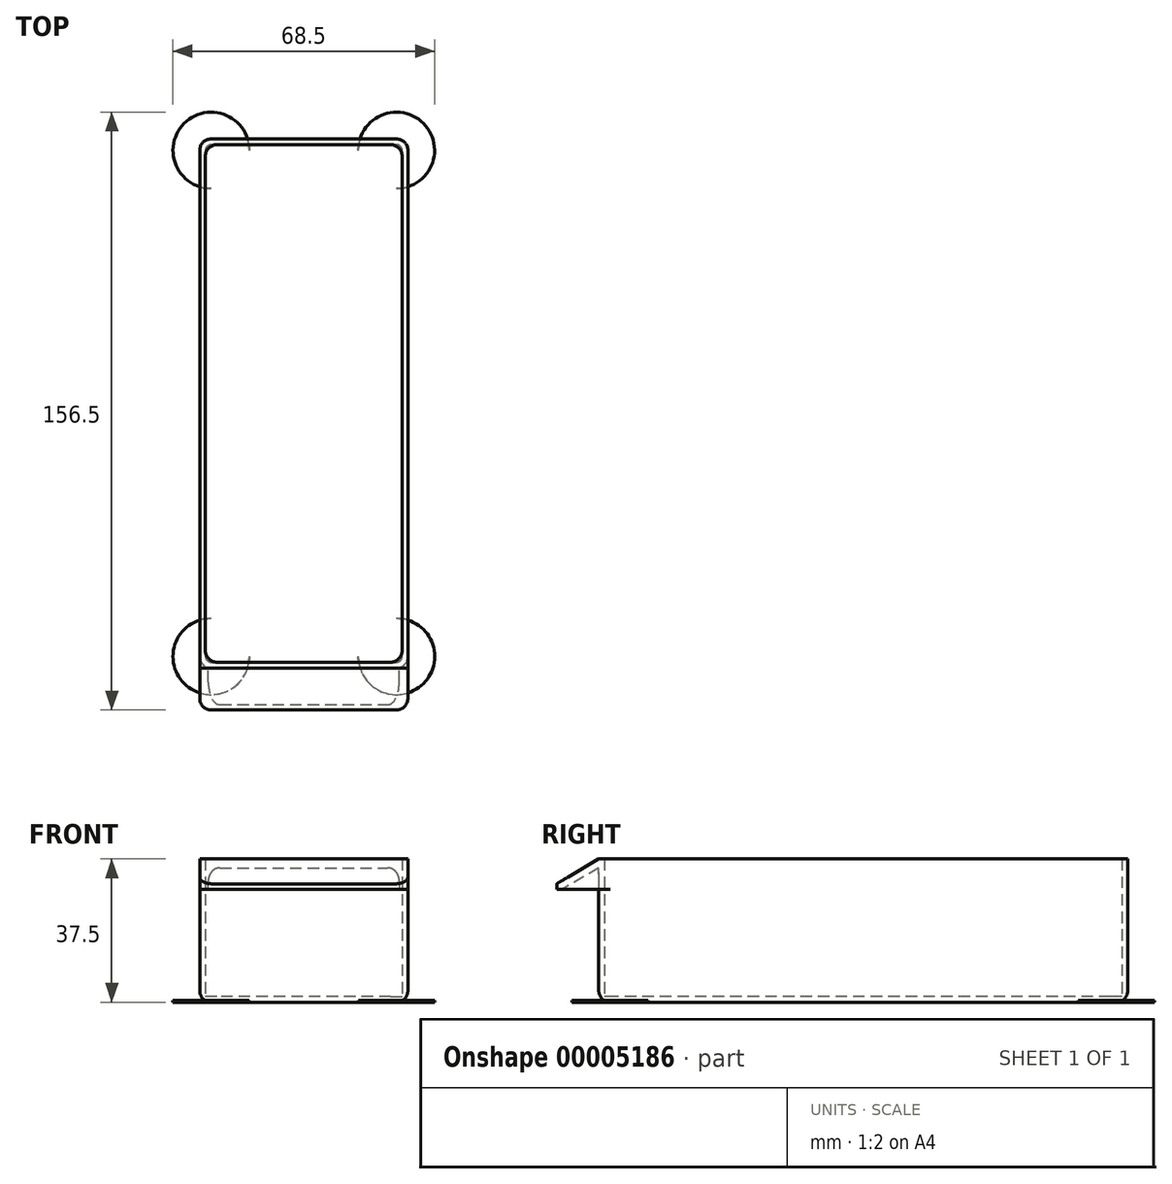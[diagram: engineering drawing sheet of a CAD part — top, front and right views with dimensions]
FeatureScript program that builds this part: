
annotation { "Feature Type Name" : "Feature", "Feature Type Description" : "" }
export const myFeature = defineFeature(function(context is Context, id is Id, definition is map)
    precondition{}
    {
        {
            var Q0;
            Q0=qCreatedBy(makeId("Top.planeOp"),FACE);
            var sketch = newSketch(context, id + "F0", { "sketchPlane" : qUnion([Q0])});
            skLineSegment(sketch, "E0.bottom", {"start": v(27.25, 69.25) * mm, "end": v(-27.25, 69.25) * mm});
            skLineSegment(sketch, "E0.top", {"start": v(27.25, -69.25) * mm, "end": v(-27.25, -69.25) * mm});
            skLineSegment(sketch, "E0.left", {"start": v(27.25, 69.25) * mm, "end": v(27.25, -69.25) * mm});
            skLineSegment(sketch, "E0.right", {"start": v(-27.25, 69.25) * mm, "end": v(-27.25, -69.25) * mm});
            skPoint(sketch, "E0.middle", {"position": v(0, 0) * mm});
            skSolve(sketch);
        }
        {
            var Q0;
            Q0 = qSketchRegion(id + "F0", true);
            extrude(context, id + "F1", {"entities" : qUnion([Q0]), "depth" : 1.5 * mm});
        }
        {
            var Q0;
            Q0=makeQuery(id+"F1.opExtrude","CAP_FACE",FACE,{"disambiguationData":[OSD([sQuery(id+"F0.wireOp",EDGE,"E0.bottom"),sQuery(id+"F0.wireOp",EDGE,"E0.top"),sQuery(id+"F0.wireOp",EDGE,"E0.left"),sQuery(id+"F0.wireOp",EDGE,"E0.right")])],"isStart":false});
            var sketch = newSketch(context, id + "F2", { "sketchPlane" : qUnion([Q0])});
            skLineSegment(sketch, "E1.0", {"start": v(27.25, 69.25) * mm, "end": v(-27.25, 69.25) * mm});
            skLineSegment(sketch, "E1.1", {"start": v(-27.25, 69.25) * mm, "end": v(-27.25, -69.25) * mm});
            skLineSegment(sketch, "E1.2", {"start": v(27.25, 69.25) * mm, "end": v(27.25, -69.25) * mm});
            skLineSegment(sketch, "E1.3", {"start": v(27.25, -69.25) * mm, "end": v(-27.25, -69.25) * mm});
            skLineSegment(sketch, "E2.bottom", {"start": v(25.75, 67.75) * mm, "end": v(-25.75, 67.75) * mm});
            skLineSegment(sketch, "E2.top", {"start": v(25.75, -67.75) * mm, "end": v(-25.75, -67.75) * mm});
            skLineSegment(sketch, "E2.left", {"start": v(25.75, 67.75) * mm, "end": v(25.75, -67.75) * mm});
            skLineSegment(sketch, "E2.right", {"start": v(-25.75, 67.75) * mm, "end": v(-25.75, -67.75) * mm});
            skPoint(sketch, "E2.middle", {"position": v(0, 0) * mm});
            skSolve(sketch);
        }
        {
            var Q0;
            Q0 = qSketchRegion(id + "F2", true);
            extrude(context, id + "F3", {"entities" : qUnion([Q0]), "operationType" : NewBodyOperationType.ADD, "depth" : 36 * mm});
        }
        {
            var Q0;
            Q0=makeQuery(id+"F3.boolean.opBoolean","MERGE",FACE,{"derivedFrom":[makeQuery(id+"F1.opExtrude","SWEPT_FACE",FACE,{"disambiguationData":[OSD([sQuery(id+"F0.wireOp",EDGE,"E0.right")])]}),makeQuery(id+"F3.opExtrude","SWEPT_FACE",FACE,{"disambiguationData":[OSD([sQuery(id+"F2.wireOp",EDGE,"E1.1")])]})]});
            var sketch = newSketch(context, id + "F4", { "sketchPlane" : qUnion([Q0])});
            skLineSegment(sketch, "E3", {"start": v(69.25, 37.5) * mm, "end": v(80.25, 31) * mm});
            skLineSegment(sketch, "E4", {"start": v(80.25, 31) * mm, "end": v(80.25, 29.5) * mm});
            skLineSegment(sketch, "E5", {"start": v(80.25, 29.5) * mm, "end": v(69.25, 29.5) * mm});
            skLineSegment(sketch, "E6", {"start": v(69.25, 29.5) * mm, "end": v(69.25, 37.5) * mm});
            skSolve(sketch);
        }
        {
            var Q0;
            Q0 = qSketchRegion(id + "F4", true);
            var Q1;
            Q1=makeQuery(id+"F3.boolean.opBoolean","MERGE",FACE,{"derivedFrom":[makeQuery(id+"F1.opExtrude","SWEPT_FACE",FACE,{"disambiguationData":[OSD([sQuery(id+"F0.wireOp",EDGE,"E0.left")])]}),makeQuery(id+"F3.opExtrude","SWEPT_FACE",FACE,{"disambiguationData":[OSD([sQuery(id+"F2.wireOp",EDGE,"E1.2")])]})]});
            extrude(context, id + "F5", {"entities" : qUnion([Q0]), "operationType" : NewBodyOperationType.ADD, "endBound" : BoundingType.UP_TO_SURFACE, "oppositeDirection" : true, "endBoundEntityFace" : qUnion([Q1]), "depth" : 25 * mm});
        }
        {
            var Q0;
            Q0=qCreatedBy(makeId("Right.planeOp"),FACE);
            var sketch = newSketch(context, id + "F6", { "sketchPlane" : qUnion([Q0])});
            skLineSegment(sketch, "E7.0", {"start": v(-69.25, 37.5) * mm, "end": v(-80.25, 31) * mm, "construction": true});
            skLineSegment(sketch, "E7.1", {"start": v(-80.25, 29.5) * mm, "end": v(-69.25, 29.5) * mm, "construction": true});
            skLineSegment(sketch, "E8", {"start": v(-69.25, 35.18) * mm, "end": v(-78.86, 29.5) * mm});
            skLineSegment(sketch, "E9", {"start": v(-78.86, 29.5) * mm, "end": v(-69.25, 29.5) * mm});
            skLineSegment(sketch, "E10", {"start": v(-69.25, 35.18) * mm, "end": v(-69.25, 29.5) * mm});
            skSolve(sketch);
        }
        {
            var Q0;
            Q0 = qSketchRegion(id + "F6", true);
            extrude(context, id + "F7", {"entities" : qUnion([Q0]), "operationType" : NewBodyOperationType.REMOVE, "oppositeDirection" : true, "depth" : 50 * mm, "symmetric" : true});
        }
        {
            var Q0;
            Q0=makeQuery(id+"F3.boolean.opBoolean","MERGE",EDGE,{"derivedFrom":[makeQuery(id+"F1.opExtrude","SWEPT_EDGE",EDGE,{"disambiguationData":[OSD([sQuery(id+"F0.wireOp",EDGE,"E0.top"),sQuery(id+"F0.wireOp",EDGE,"E0.right")])]}),makeQuery(id+"F3.opExtrude","SWEPT_EDGE",EDGE,{"disambiguationData":[OSD([sQuery(id+"F2.wireOp",EDGE,"E1.1"),sQuery(id+"F2.wireOp",EDGE,"E1.3")])]})]});
            var Q1;
            Q1=makeQuery(id+"F3.boolean.opBoolean","MERGE",EDGE,{"derivedFrom":[makeQuery(id+"F1.opExtrude","SWEPT_EDGE",EDGE,{"disambiguationData":[OSD([sQuery(id+"F0.wireOp",EDGE,"E0.top"),sQuery(id+"F0.wireOp",EDGE,"E0.left")])]}),makeQuery(id+"F3.opExtrude","SWEPT_EDGE",EDGE,{"disambiguationData":[OSD([sQuery(id+"F2.wireOp",EDGE,"E1.2"),sQuery(id+"F2.wireOp",EDGE,"E1.3")])]})]});
            var Q2;
            Q2=makeQuery(id+"F3.opExtrude","SWEPT_EDGE",EDGE,{"disambiguationData":[OSD([sQuery(id+"F2.wireOp",EDGE,"E2.top"),sQuery(id+"F2.wireOp",EDGE,"E2.left")])]});
            var Q3;
            Q3=makeQuery(id+"F3.opExtrude","SWEPT_EDGE",EDGE,{"disambiguationData":[OSD([sQuery(id+"F2.wireOp",EDGE,"E2.top"),sQuery(id+"F2.wireOp",EDGE,"E2.right")])]});
            var Q4;
            Q4=makeQuery(id+"F3.boolean.opBoolean","MERGE",EDGE,{"derivedFrom":[makeQuery(id+"F1.opExtrude","SWEPT_EDGE",EDGE,{"disambiguationData":[OSD([sQuery(id+"F0.wireOp",EDGE,"E0.bottom"),sQuery(id+"F0.wireOp",EDGE,"E0.left")])]}),makeQuery(id+"F3.opExtrude","SWEPT_EDGE",EDGE,{"disambiguationData":[OSD([sQuery(id+"F2.wireOp",EDGE,"E1.0"),sQuery(id+"F2.wireOp",EDGE,"E1.2")])]})]});
            var Q5;
            Q5=makeQuery(id+"F3.boolean.opBoolean","MERGE",EDGE,{"derivedFrom":[makeQuery(id+"F1.opExtrude","SWEPT_EDGE",EDGE,{"disambiguationData":[OSD([sQuery(id+"F0.wireOp",EDGE,"E0.bottom"),sQuery(id+"F0.wireOp",EDGE,"E0.right")])]}),makeQuery(id+"F3.opExtrude","SWEPT_EDGE",EDGE,{"disambiguationData":[OSD([sQuery(id+"F2.wireOp",EDGE,"E1.0"),sQuery(id+"F2.wireOp",EDGE,"E1.1")])]})]});
            var Q6;
            Q6=makeQuery(id+"F3.opExtrude","SWEPT_EDGE",EDGE,{"disambiguationData":[OSD([sQuery(id+"F2.wireOp",EDGE,"E2.bottom"),sQuery(id+"F2.wireOp",EDGE,"E2.left")])]});
            var Q7;
            Q7=makeQuery(id+"F3.opExtrude","SWEPT_EDGE",EDGE,{"disambiguationData":[OSD([sQuery(id+"F2.wireOp",EDGE,"E2.bottom"),sQuery(id+"F2.wireOp",EDGE,"E2.right")])]});
            var Q8;
            Q8=makeQuery(id+"F1.opExtrude","CAP_EDGE",EDGE,{"disambiguationData":[OSD([sQuery(id+"F0.wireOp",EDGE,"E0.right")])],"isStart":true});
            var Q9;
            Q9=makeQuery(id+"F1.opExtrude","CAP_EDGE",EDGE,{"disambiguationData":[OSD([sQuery(id+"F0.wireOp",EDGE,"E0.bottom")])],"isStart":true});
            var Q10;
            Q10=makeQuery(id+"F1.opExtrude","CAP_EDGE",EDGE,{"disambiguationData":[OSD([sQuery(id+"F0.wireOp",EDGE,"E0.left")])],"isStart":true});
            var Q11;
            Q11=makeQuery(id+"F1.opExtrude","CAP_EDGE",EDGE,{"disambiguationData":[OSD([sQuery(id+"F0.wireOp",EDGE,"E0.top")])],"isStart":true});
            var Q12;
            Q12=makeQuery(id+"F5.opExtrude","CAP_EDGE",EDGE,{"disambiguationData":[OSD([sQuery(id+"F4.wireOp",EDGE,"E4")])],"isStart":true});
            var Q13;
            Q13=makeQuery(id+"F5.opExtrude","CAP_EDGE",EDGE,{"disambiguationData":[OSD([sQuery(id+"F4.wireOp",EDGE,"E4")])],"isStart":false});
            var Q14;
            Q14=makeQuery(id+"F7.boolean.opBoolean","COPY",EDGE,{"derivedFrom":makeQuery(id+"F7.opExtrude","CAP_EDGE",EDGE,{"disambiguationData":[OSD([sQuery(id+"F6.wireOp",EDGE,"E8")])],"isStart":true})});
            var Q15;
            Q15=makeQuery(id+"F7.boolean.opBoolean","COPY",EDGE,{"derivedFrom":makeQuery(id+"F7.opExtrude","CAP_EDGE",EDGE,{"disambiguationData":[OSD([sQuery(id+"F6.wireOp",EDGE,"E8")])],"isStart":false})});
            var Q16;
            Q16=makeQuery(id+"F3.opExtrude","CAP_EDGE",EDGE,{"disambiguationData":[OSD([sQuery(id+"F2.wireOp",EDGE,"E2.bottom")])],"isStart":true});
            var Q17;
            Q17=makeQuery(id+"F3.opExtrude","CAP_EDGE",EDGE,{"disambiguationData":[OSD([sQuery(id+"F2.wireOp",EDGE,"E2.left")])],"isStart":true});
            var Q18;
            Q18=makeQuery(id+"F3.opExtrude","CAP_EDGE",EDGE,{"disambiguationData":[OSD([sQuery(id+"F2.wireOp",EDGE,"E2.right")])],"isStart":true});
            var Q19;
            Q19=makeQuery(id+"F3.opExtrude","CAP_EDGE",EDGE,{"disambiguationData":[OSD([sQuery(id+"F2.wireOp",EDGE,"E2.top")])],"isStart":true});
            fillet(context, id + "F8", {"entities" : qUnion([Q0, Q1, Q2, Q3, Q4, Q5, Q6, Q7, Q8, Q9, Q10, Q11, Q12, Q13, Q14, Q15, Q16, Q17, Q18, Q19]), "radius" : 3 * mm, "tangentPropagation" : true, "allowEdgeOverflow" : false});
        }
        {
            var Q0;
            Q0=makeQuery(id+"F1.opExtrude","CAP_FACE",FACE,{"disambiguationData":[OSD([sQuery(id+"F0.wireOp",EDGE,"E0.bottom"),sQuery(id+"F0.wireOp",EDGE,"E0.top"),sQuery(id+"F0.wireOp",EDGE,"E0.left"),sQuery(id+"F0.wireOp",EDGE,"E0.right")])],"isStart":true});
            var sketch = newSketch(context, id + "F9", { "sketchPlane" : qUnion([Q0])});
            skCircle(sketch, "E11", {"center": v(-24.25, 66.25) * mm, "radius": 10 * mm});
            skCircle(sketch, "E12", {"center": v(24.25, 66.25) * mm, "radius": 10 * mm});
            skCircle(sketch, "E13", {"center": v(-24.25, -66.25) * mm, "radius": 10 * mm});
            skCircle(sketch, "E14", {"center": v(24.25, -66.25) * mm, "radius": 10 * mm});
            skSolve(sketch);
        }
        {
            var Q0;
            Q0 = qSketchRegion(id + "F9", true);
            extrude(context, id + "F10", {"entities" : qUnion([Q0]), "operationType" : NewBodyOperationType.ADD, "oppositeDirection" : true, "depth" : 0.4 * mm});
        }
    });
